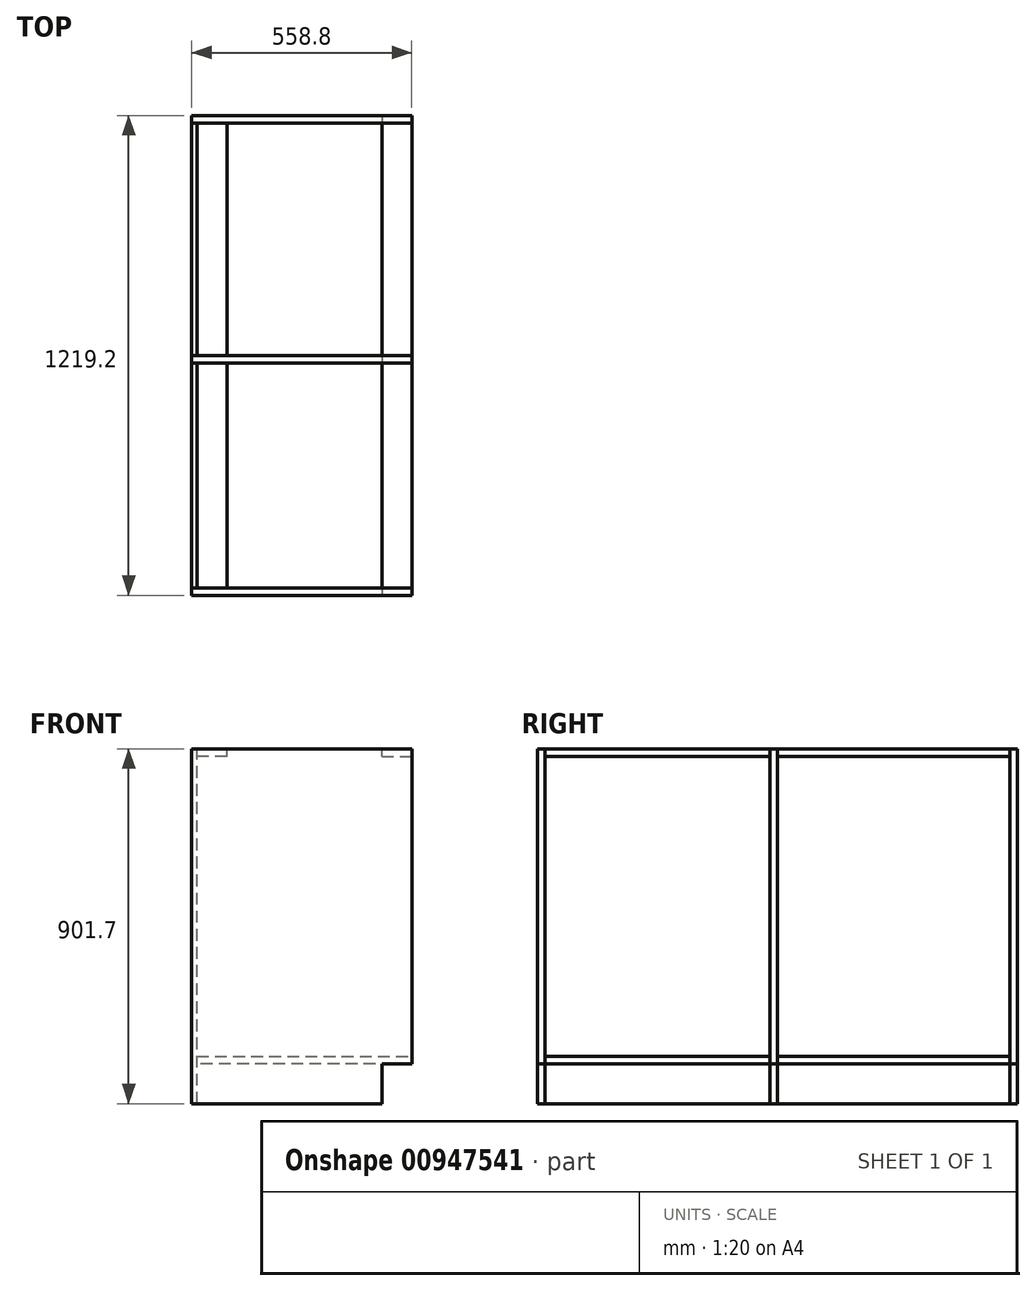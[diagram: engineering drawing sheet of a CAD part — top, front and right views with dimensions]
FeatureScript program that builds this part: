
annotation { "Feature Type Name" : "Feature", "Feature Type Description" : "" }
export const myFeature = defineFeature(function(context is Context, id is Id, definition is map)
    precondition{}
    {
        {
            var Q0;
            Q0=qCreatedBy(makeId("Top.planeOp"),FACE);
            var sketch = newSketch(context, id + "F0", { "sketchPlane" : qUnion([Q0])});
            skLineSegment(sketch, "E0", {"start": v(-384.18, 0) * mm, "end": v(-1247.78, 0) * mm});
            skLineSegment(sketch, "E1", {"start": v(-1247.78, 0) * mm, "end": v(-1247.78, 2298.7) * mm});
            skLineSegment(sketch, "E2", {"start": v(-1247.78, 2298.7) * mm, "end": v(206.37, 2298.7) * mm});
            skLineSegment(sketch, "E3", {"start": v(206.37, 2298.7) * mm, "end": v(206.37, 1555.75) * mm});
            skLineSegment(sketch, "E4", {"start": v(206.37, 1555.75) * mm, "end": v(574.68, 1555.75) * mm});
            skLineSegment(sketch, "E5", {"start": v(574.68, 1555.75) * mm, "end": v(574.68, 0) * mm});
            skLineSegment(sketch, "E6", {"start": v(574.68, 0) * mm, "end": v(384.18, 0) * mm});
            skLineSegment(sketch, "E7", {"start": v(384.18, 0) * mm, "end": v(-384.18, 0) * mm});
            skLineSegment(sketch, "E8", {"start": v(-1171.58, 0) * mm, "end": v(-1171.58, -45.45) * mm, "construction": true});
            skLineSegment(sketch, "E9", {"start": v(-1171.58, -45.45) * mm, "end": v(-892.17, -45.45) * mm, "construction": true});
            skLineSegment(sketch, "E10", {"start": v(-892.17, -45.45) * mm, "end": v(-892.17, 0) * mm, "construction": true});
            skLineSegment(sketch, "E11", {"start": v(-1247.78, 457.2) * mm, "end": v(-973.1, 457.2) * mm, "construction": true});
            skLineSegment(sketch, "E12", {"start": v(206.37, 1555.75) * mm, "end": v(-1247.78, 1555.75) * mm, "construction": true});
            skLineSegment(sketch, "E13", {"start": v(-1247.78, 1219.2) * mm, "end": v(-688.98, 1219.2) * mm, "construction": true});
            skLineSegment(sketch, "E14", {"start": v(-688.98, 1219.2) * mm, "end": v(-688.97, 0) * mm, "construction": true});
            skCircle(sketch, "E15", {"center": v(-982.78, 355.6) * mm, "radius": 168.58 * mm});
            skLineSegment(sketch, "E16", {"start": v(-688.98, 609.6) * mm, "end": v(-1247.78, 609.6) * mm, "construction": true});
            skSolve(sketch);
        }
        {
            var Q0;
            Q0=sQuery(id+"F0.wireOp",EDGE,"E0");
            var Q1;
            Q1=sQuery(id+"F0.wireOp",VERTEX,"E0.end");
            cPlane(context, id + "F1", {"entities" : qUnion([Q0, Q1]), "cplaneType" : CPlaneType.LINE_POINT, "offset" : 25.4 * mm, "width" : 152.4 * mm, "height" : 152.4 * mm});
        }
        {
            var Q0;
            Q0=qCreatedBy(makeId("Front.planeOp"),FACE);
            var sketch = newSketch(context, id + "F2", { "sketchPlane" : qUnion([Q0])});
            skLineSegment(sketch, "E17", {"start": v(-1247.78, 0) * mm, "end": v(-765.17, 0) * mm});
            skLineSegment(sketch, "E18", {"start": v(-765.17, 0) * mm, "end": v(-765.17, 101.6) * mm});
            skLineSegment(sketch, "E19", {"start": v(-765.17, 101.6) * mm, "end": v(-688.97, 101.6) * mm});
            skLineSegment(sketch, "E20", {"start": v(-688.97, 101.6) * mm, "end": v(-688.98, 901.7) * mm});
            skLineSegment(sketch, "E21", {"start": v(-688.97, 901.7) * mm, "end": v(-1247.78, 901.7) * mm});
            skLineSegment(sketch, "E22", {"start": v(-1247.78, 901.7) * mm, "end": v(-1247.78, 0) * mm});
            skSolve(sketch);
        }
        {
            var Q0;
            Q0 = qSketchRegion(id + "F2", true);
            extrude(context, id + "F3", {"entities" : qUnion([Q0]), "oppositeDirection" : true, "depth" : 19.05 * mm, "offsetDistance" : 25.4 * mm});
        }
        {
            var Q0;
            Q0=makeQuery(id+"F3.opExtrude","SWEPT_BODY",BODY,{"disambiguationData":[OSD([sQuery(id+"F2.wireOp",EDGE,"E17"),sQuery(id+"F2.wireOp",EDGE,"E18"),sQuery(id+"F2.wireOp",EDGE,"E19"),sQuery(id+"F2.wireOp",EDGE,"E20"),sQuery(id+"F2.wireOp",EDGE,"E21"),sQuery(id+"F2.wireOp",EDGE,"E22")])]});
            transform(context, id + "F4", {"entities" : qUnion([Q0]), "transformType" : TransformType.TRANSLATION_3D, "dx" : 0 * mm, "dy" : 590.55 * mm, "dz" : 0 * mm, "makeCopy" : true});
        }
        {
            var Q0;
            Q0=makeQuery(id+"F4.opPattern","COPY",BODY,{"derivedFrom":makeQuery(id+"F3.opExtrude","SWEPT_BODY",BODY,{"disambiguationData":[OSD([sQuery(id+"F2.wireOp",EDGE,"E17"),sQuery(id+"F2.wireOp",EDGE,"E18"),sQuery(id+"F2.wireOp",EDGE,"E19"),sQuery(id+"F2.wireOp",EDGE,"E20"),sQuery(id+"F2.wireOp",EDGE,"E21"),sQuery(id+"F2.wireOp",EDGE,"E22")])]}),"instanceName":"1"});
            transform(context, id + "F5", {"entities" : qUnion([Q0]), "transformType" : TransformType.TRANSLATION_3D, "dx" : 0 * mm, "dy" : 609.6 * mm, "dz" : 0 * mm, "makeCopy" : true});
        }
        {
            var Q0;
            Q0=makeQuery(id+"F3.opExtrude","CAP_FACE",FACE,{"disambiguationData":[OSD([sQuery(id+"F2.wireOp",EDGE,"E17"),sQuery(id+"F2.wireOp",EDGE,"E18"),sQuery(id+"F2.wireOp",EDGE,"E19"),sQuery(id+"F2.wireOp",EDGE,"E20"),sQuery(id+"F2.wireOp",EDGE,"E21"),sQuery(id+"F2.wireOp",EDGE,"E22")])],"isStart":false});
            var sketch = newSketch(context, id + "F6", { "sketchPlane" : qUnion([Q0])});
            skLineSegment(sketch, "E23.bottom", {"start": v(688.98, 901.7) * mm, "end": v(765.18, 901.7) * mm});
            skLineSegment(sketch, "E23.top", {"start": v(688.98, 882.65) * mm, "end": v(765.18, 882.65) * mm});
            skLineSegment(sketch, "E23.left", {"start": v(688.98, 901.7) * mm, "end": v(688.98, 882.65) * mm});
            skLineSegment(sketch, "E23.right", {"start": v(765.18, 901.7) * mm, "end": v(765.18, 882.65) * mm});
            skLineSegment(sketch, "E24.bottom", {"start": v(1235.08, 901.7) * mm, "end": v(1158.88, 901.7) * mm});
            skLineSegment(sketch, "E24.top", {"start": v(1235.08, 882.65) * mm, "end": v(1158.88, 882.65) * mm});
            skLineSegment(sketch, "E24.left", {"start": v(1235.08, 901.7) * mm, "end": v(1235.08, 882.65) * mm});
            skLineSegment(sketch, "E24.right", {"start": v(1158.88, 901.7) * mm, "end": v(1158.88, 882.65) * mm});
            skLineSegment(sketch, "E25.bottom", {"start": v(688.97, 101.6) * mm, "end": v(1235.08, 101.6) * mm});
            skLineSegment(sketch, "E25.top", {"start": v(688.97, 120.65) * mm, "end": v(1235.08, 120.65) * mm});
            skLineSegment(sketch, "E25.left", {"start": v(688.97, 101.6) * mm, "end": v(688.97, 120.65) * mm});
            skLineSegment(sketch, "E26", {"start": v(1235.08, 120.65) * mm, "end": v(1235.08, 101.6) * mm});
            skSolve(sketch);
        }
        {
            var Q0;
            Q0 = qSketchRegion(id + "F6", true);
            var Q1;
            Q1=makeQuery(id+"F4.opPattern","COPY",FACE,{"derivedFrom":makeQuery(id+"F3.opExtrude","CAP_FACE",FACE,{"disambiguationData":[OSD([sQuery(id+"F2.wireOp",EDGE,"E17"),sQuery(id+"F2.wireOp",EDGE,"E18"),sQuery(id+"F2.wireOp",EDGE,"E19"),sQuery(id+"F2.wireOp",EDGE,"E20"),sQuery(id+"F2.wireOp",EDGE,"E21"),sQuery(id+"F2.wireOp",EDGE,"E22")])],"isStart":true}),"instanceName":"1"});
            extrude(context, id + "F7", {"entities" : qUnion([Q0]), "endBound" : BoundingType.UP_TO_SURFACE, "depth" : 25.4 * mm, "endBoundEntityFace" : qUnion([Q1]), "offsetDistance" : 25.4 * mm});
        }
        {
            var Q0;
            Q0=makeQuery(id+"F4.opPattern","COPY",FACE,{"derivedFrom":makeQuery(id+"F3.opExtrude","CAP_FACE",FACE,{"disambiguationData":[OSD([sQuery(id+"F2.wireOp",EDGE,"E17"),sQuery(id+"F2.wireOp",EDGE,"E18"),sQuery(id+"F2.wireOp",EDGE,"E19"),sQuery(id+"F2.wireOp",EDGE,"E20"),sQuery(id+"F2.wireOp",EDGE,"E21"),sQuery(id+"F2.wireOp",EDGE,"E22")])],"isStart":false}),"instanceName":"1"});
            var sketch = newSketch(context, id + "F8", { "sketchPlane" : qUnion([Q0])});
            skLineSegment(sketch, "E27.bottom", {"start": v(688.98, 901.7) * mm, "end": v(765.18, 901.7) * mm});
            skLineSegment(sketch, "E27.top", {"start": v(688.98, 882.65) * mm, "end": v(765.18, 882.65) * mm});
            skLineSegment(sketch, "E27.left", {"start": v(688.98, 901.7) * mm, "end": v(688.98, 882.65) * mm});
            skLineSegment(sketch, "E27.right", {"start": v(765.18, 901.7) * mm, "end": v(765.18, 882.65) * mm});
            skLineSegment(sketch, "E28.bottom", {"start": v(1235.08, 901.7) * mm, "end": v(1158.88, 901.7) * mm});
            skLineSegment(sketch, "E28.top", {"start": v(1235.08, 882.65) * mm, "end": v(1158.88, 882.65) * mm});
            skLineSegment(sketch, "E28.right", {"start": v(1158.88, 901.7) * mm, "end": v(1158.88, 882.65) * mm});
            skLineSegment(sketch, "E29.bottom", {"start": v(688.98, 101.6) * mm, "end": v(1235.08, 101.6) * mm});
            skLineSegment(sketch, "E29.top", {"start": v(688.97, 120.65) * mm, "end": v(1235.08, 120.65) * mm});
            skLineSegment(sketch, "E29.left", {"start": v(688.97, 101.6) * mm, "end": v(688.97, 120.65) * mm});
            skLineSegment(sketch, "E30", {"start": v(1235.08, 901.7) * mm, "end": v(1235.08, 882.65) * mm});
            skLineSegment(sketch, "E31", {"start": v(1235.08, 120.65) * mm, "end": v(1235.08, 101.6) * mm});
            skSolve(sketch);
        }
        {
            var Q0;
            Q0 = qSketchRegion(id + "F8", true);
            var Q1;
            Q1=makeQuery(id+"F5.opPattern","COPY",FACE,{"derivedFrom":makeQuery(id+"F4.opPattern","COPY",FACE,{"derivedFrom":makeQuery(id+"F3.opExtrude","CAP_FACE",FACE,{"disambiguationData":[OSD([sQuery(id+"F2.wireOp",EDGE,"E17"),sQuery(id+"F2.wireOp",EDGE,"E18"),sQuery(id+"F2.wireOp",EDGE,"E19"),sQuery(id+"F2.wireOp",EDGE,"E20"),sQuery(id+"F2.wireOp",EDGE,"E21"),sQuery(id+"F2.wireOp",EDGE,"E22")])],"isStart":true}),"instanceName":"1"}),"instanceName":"1"});
            extrude(context, id + "F9", {"entities" : qUnion([Q0]), "endBound" : BoundingType.UP_TO_SURFACE, "depth" : 25.4 * mm, "endBoundEntityFace" : qUnion([Q1]), "offsetDistance" : 25.4 * mm});
        }
        {
            var Q0;
            Q0=makeQuery(id+"F3.opExtrude","CAP_FACE",FACE,{"disambiguationData":[OSD([sQuery(id+"F2.wireOp",EDGE,"E17"),sQuery(id+"F2.wireOp",EDGE,"E18"),sQuery(id+"F2.wireOp",EDGE,"E19"),sQuery(id+"F2.wireOp",EDGE,"E20"),sQuery(id+"F2.wireOp",EDGE,"E21"),sQuery(id+"F2.wireOp",EDGE,"E22")])],"isStart":false});
            var sketch = newSketch(context, id + "F10", { "sketchPlane" : qUnion([Q0])});
            skLineSegment(sketch, "E32.bottom", {"start": v(1247.78, 901.7) * mm, "end": v(1235.07, 901.7) * mm});
            skLineSegment(sketch, "E32.top", {"start": v(1247.78, 0) * mm, "end": v(1235.08, 0) * mm});
            skLineSegment(sketch, "E32.left", {"start": v(1247.78, 901.7) * mm, "end": v(1247.78, 0) * mm});
            skLineSegment(sketch, "E32.right", {"start": v(1235.07, 901.7) * mm, "end": v(1235.08, 0) * mm});
            skSolve(sketch);
        }
        {
            var Q0;
            Q0 = qSketchRegion(id + "F10", true);
            var Q1;
            Q1=makeQuery(id+"F4.opPattern","COPY",FACE,{"derivedFrom":makeQuery(id+"F3.opExtrude","CAP_FACE",FACE,{"disambiguationData":[OSD([sQuery(id+"F2.wireOp",EDGE,"E17"),sQuery(id+"F2.wireOp",EDGE,"E18"),sQuery(id+"F2.wireOp",EDGE,"E19"),sQuery(id+"F2.wireOp",EDGE,"E20"),sQuery(id+"F2.wireOp",EDGE,"E21"),sQuery(id+"F2.wireOp",EDGE,"E22")])],"isStart":true}),"instanceName":"1"});
            extrude(context, id + "F11", {"entities" : qUnion([Q0]), "endBound" : BoundingType.UP_TO_SURFACE, "depth" : 25.4 * mm, "endBoundEntityFace" : qUnion([Q1]), "offsetDistance" : 25.4 * mm});
        }
        {
            var Q0;
            Q0=makeQuery(id+"F4.opPattern","COPY",FACE,{"derivedFrom":makeQuery(id+"F3.opExtrude","CAP_FACE",FACE,{"disambiguationData":[OSD([sQuery(id+"F2.wireOp",EDGE,"E17"),sQuery(id+"F2.wireOp",EDGE,"E18"),sQuery(id+"F2.wireOp",EDGE,"E19"),sQuery(id+"F2.wireOp",EDGE,"E20"),sQuery(id+"F2.wireOp",EDGE,"E21"),sQuery(id+"F2.wireOp",EDGE,"E22")])],"isStart":false}),"instanceName":"1"});
            var sketch = newSketch(context, id + "F12", { "sketchPlane" : qUnion([Q0])});
            skLineSegment(sketch, "E33.bottom", {"start": v(1247.78, 901.7) * mm, "end": v(1235.07, 901.7) * mm});
            skLineSegment(sketch, "E33.top", {"start": v(1247.78, 0) * mm, "end": v(1235.08, 0) * mm});
            skLineSegment(sketch, "E33.left", {"start": v(1247.78, 901.7) * mm, "end": v(1247.78, 0) * mm});
            skLineSegment(sketch, "E33.right", {"start": v(1235.07, 901.7) * mm, "end": v(1235.08, 0) * mm});
            skSolve(sketch);
        }
        {
            var Q0;
            Q0 = qSketchRegion(id + "F12", true);
            var Q1;
            Q1=makeQuery(id+"F5.opPattern","COPY",FACE,{"derivedFrom":makeQuery(id+"F4.opPattern","COPY",FACE,{"derivedFrom":makeQuery(id+"F3.opExtrude","CAP_FACE",FACE,{"disambiguationData":[OSD([sQuery(id+"F2.wireOp",EDGE,"E17"),sQuery(id+"F2.wireOp",EDGE,"E18"),sQuery(id+"F2.wireOp",EDGE,"E19"),sQuery(id+"F2.wireOp",EDGE,"E20"),sQuery(id+"F2.wireOp",EDGE,"E21"),sQuery(id+"F2.wireOp",EDGE,"E22")])],"isStart":true}),"instanceName":"1"}),"instanceName":"1"});
            extrude(context, id + "F13", {"entities" : qUnion([Q0]), "endBound" : BoundingType.UP_TO_SURFACE, "depth" : 25.4 * mm, "endBoundEntityFace" : qUnion([Q1]), "offsetDistance" : 25.4 * mm});
        }
    });
